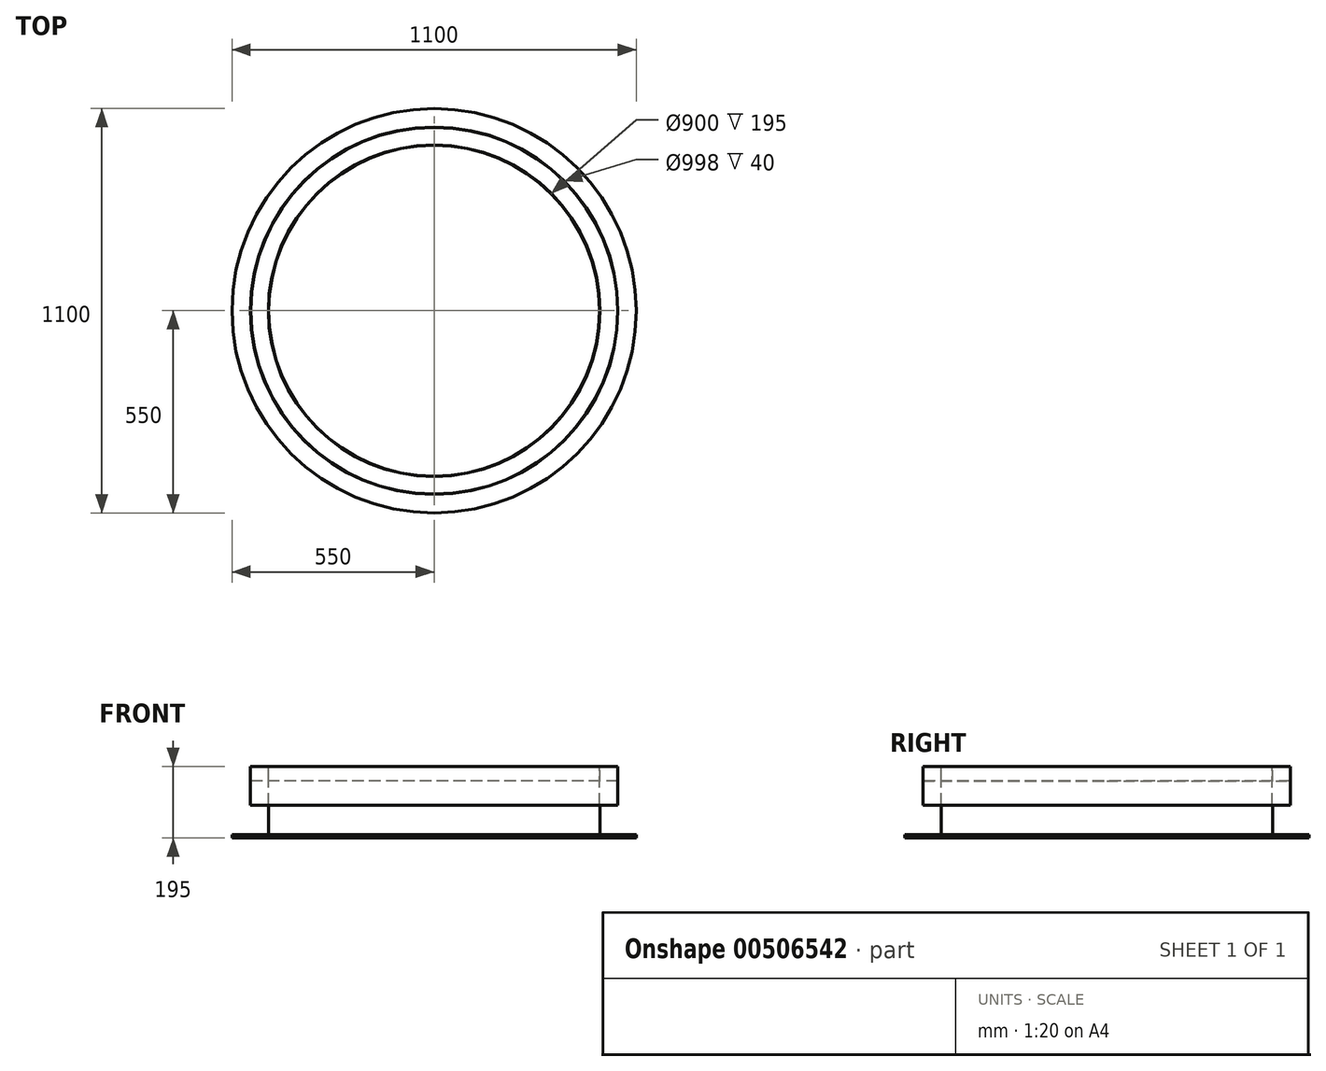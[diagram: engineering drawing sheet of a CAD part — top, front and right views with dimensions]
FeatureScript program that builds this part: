
annotation { "Feature Type Name" : "Feature", "Feature Type Description" : "" }
export const myFeature = defineFeature(function(context is Context, id is Id, definition is map)
    precondition{}
    {
        {
            var Q0;
            Q0=qCreatedBy(makeId("Front.planeOp"),FACE);
            var sketch = newSketch(context, id + "F0", { "sketchPlane" : qUnion([Q0])});
            skLineSegment(sketch, "E0", {"start": v(0, 710.75) * mm, "end": v(0, -704.58) * mm, "construction": true});
            skLineSegment(sketch, "E1", {"start": v(-450, 300.65) * mm, "end": v(-450, 495.65) * mm});
            skLineSegment(sketch, "E2", {"start": v(-450, 495.65) * mm, "end": v(-451, 495.65) * mm});
            skLineSegment(sketch, "E3", {"start": v(-499, 495.65) * mm, "end": v(-500, 495.65) * mm});
            skLineSegment(sketch, "E4", {"start": v(-500, 495.65) * mm, "end": v(-500, 390.65) * mm});
            skLineSegment(sketch, "E5", {"start": v(-500, 390.65) * mm, "end": v(-451, 390.65) * mm});
            skLineSegment(sketch, "E6", {"start": v(-451, 390.65) * mm, "end": v(-451, 310.65) * mm});
            skLineSegment(sketch, "E7", {"start": v(-451, 310.65) * mm, "end": v(-550, 310.65) * mm});
            skLineSegment(sketch, "E8", {"start": v(-550, 310.65) * mm, "end": v(-550, 300.65) * mm});
            skLineSegment(sketch, "E9", {"start": v(-550, 300.65) * mm, "end": v(-450, 300.65) * mm});
            skLineSegment(sketch, "E10", {"start": v(-499, 495.65) * mm, "end": v(-499, 455.65) * mm});
            skLineSegment(sketch, "E11", {"start": v(-499, 455.65) * mm, "end": v(-451, 455.65) * mm});
            skLineSegment(sketch, "E12", {"start": v(-451, 455.65) * mm, "end": v(-451, 495.65) * mm});
            skSolve(sketch);
        }
        {
            var Q0;
            Q0=qSketchRegion(id+"F0",true);
            var Q1;
            Q1=sQuery(id+"F0.wireOp",EDGE,"E0");
            revolve(context, id + "F1", {"entities" : qUnion([Q0]), "axis" : qUnion([Q1]), "revolveType" : RevolveType.FULL});
        }
    });
